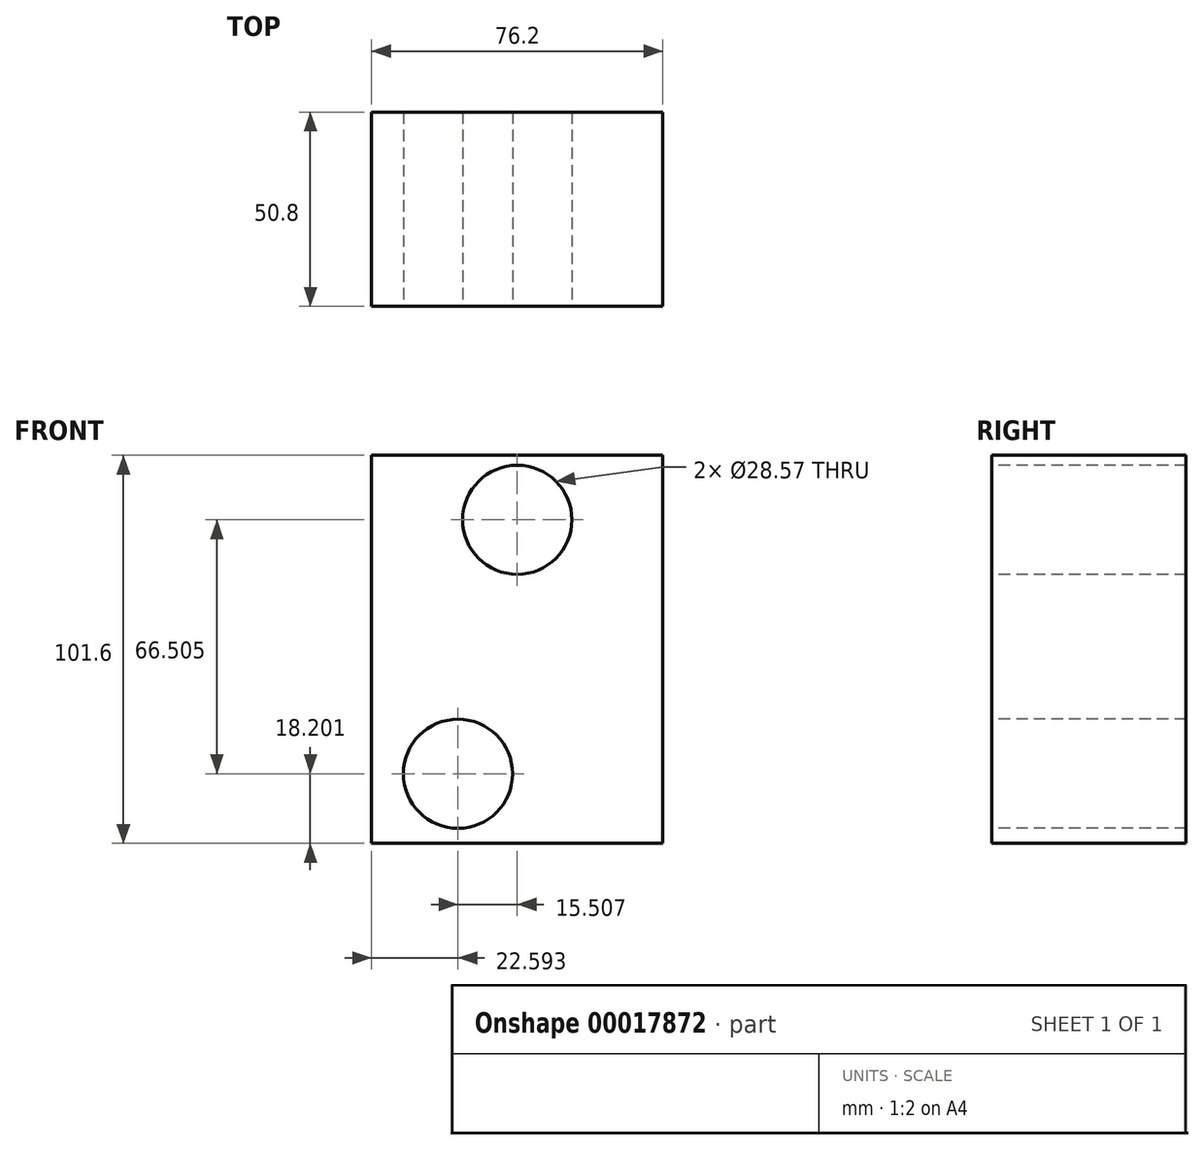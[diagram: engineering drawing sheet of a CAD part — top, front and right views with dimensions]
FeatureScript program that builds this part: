
annotation { "Feature Type Name" : "Feature", "Feature Type Description" : "" }
export const myFeature = defineFeature(function(context is Context, id is Id, definition is map)
    precondition{}
    {
        {
            var Q0;
            Q0=qCreatedBy(makeId("Top.planeOp"),FACE);
            var sketch = newSketch(context, id + "F0", { "sketchPlane" : qUnion([Q0])});
            skLineSegment(sketch, "E0.rect.bottom", {"start": v(-38.1, 25.4) * mm, "end": v(38.1, 25.4) * mm});
            skLineSegment(sketch, "E0.rect.top", {"start": v(-38.1, -25.4) * mm, "end": v(38.1, -25.4) * mm});
            skLineSegment(sketch, "E0.rect.left", {"start": v(-38.1, 25.4) * mm, "end": v(-38.1, -25.4) * mm});
            skLineSegment(sketch, "E0.rect.right", {"start": v(38.1, 25.4) * mm, "end": v(38.1, -25.4) * mm});
            skPoint(sketch, "E0.rect.middle", {"position": v(0, 0) * mm});
            skSolve(sketch);
        }
        {
            var Q0;
            Q0 = qSketchRegion(id + "F0", true);
            extrude(context, id + "F1", {"entities" : qUnion([Q0]), "depth" : 101.6 * mm});
        }
        {
            var Q0;
            Q0=makeQuery(id+"F1.opExtrude","SWEPT_FACE",FACE,{"disambiguationData":[OSD([sQuery(id+"F0.wireOp",EDGE,"E0.rect.top")])]});
            var sketch = newSketch(context, id + "F2", { "sketchPlane" : qUnion([Q0])});
            skCircle(sketch, "E1", {"center": v(0, 84.7) * mm, "radius": 14.29 * mm});
            skCircle(sketch, "E2", {"center": v(-15.5, 18.2) * mm, "radius": 14.29 * mm});
            skSolve(sketch);
        }
        {
            var Q0;
            Q0 = qSketchRegion(id + "F2", true);
            extrude(context, id + "F3", {"entities" : qUnion([Q0]), "operationType" : NewBodyOperationType.REMOVE, "endBound" : BoundingType.THROUGH_ALL, "oppositeDirection" : true, "depth" : 25.4 * mm});
        }
    });
